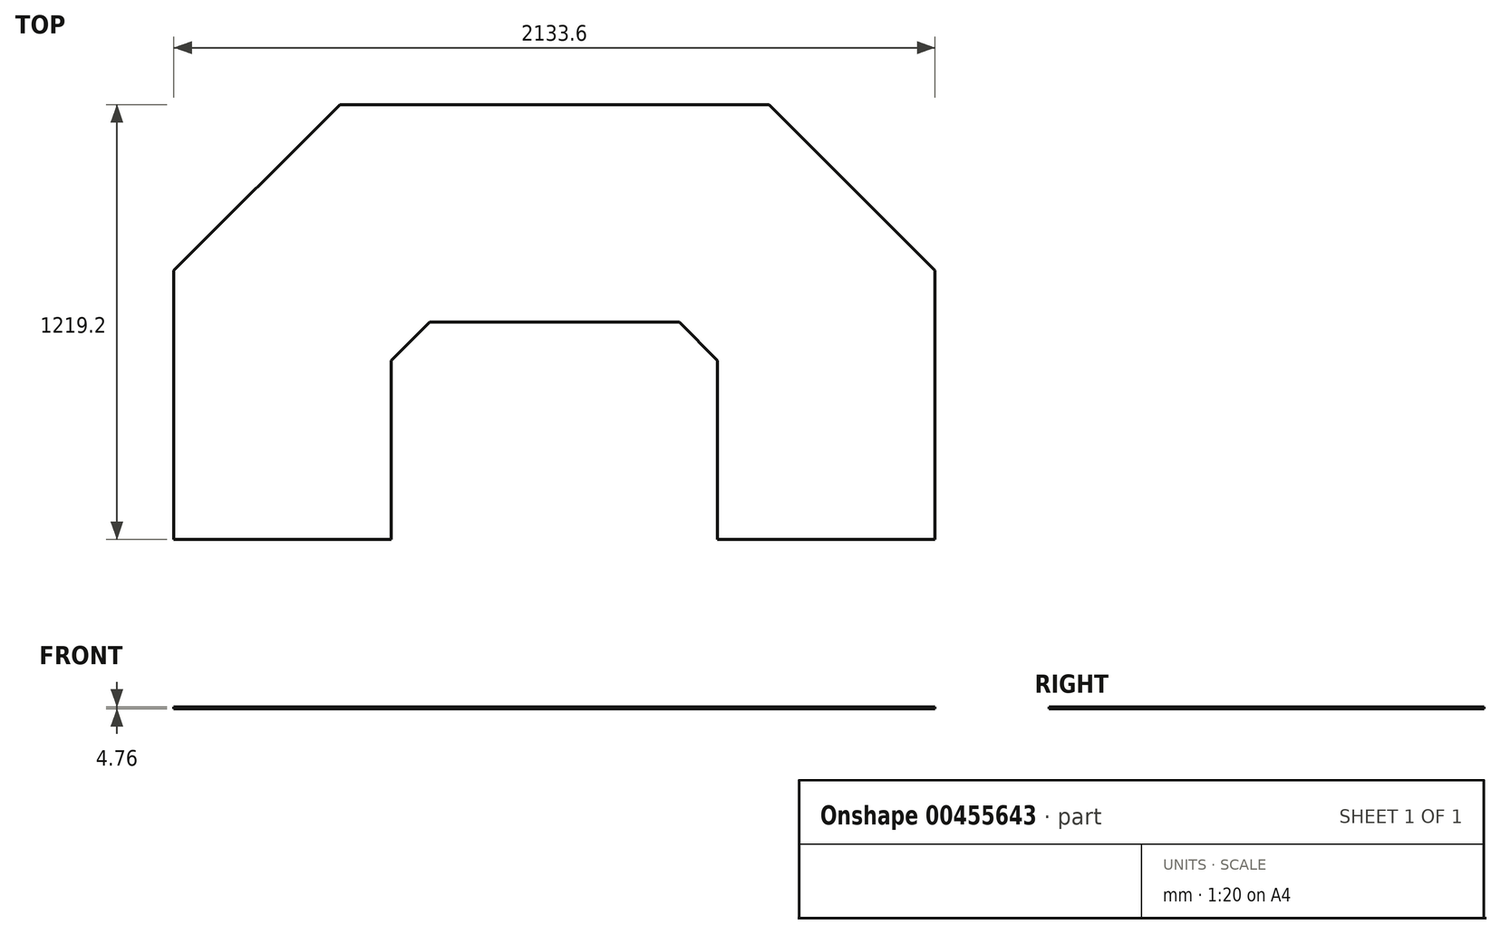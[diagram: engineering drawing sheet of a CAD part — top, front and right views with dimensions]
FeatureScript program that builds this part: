
annotation { "Feature Type Name" : "Feature", "Feature Type Description" : "" }
export const myFeature = defineFeature(function(context is Context, id is Id, definition is map)
    precondition{}
    {
        {
            var Q0;
            Q0=qCreatedBy(makeId("Top.planeOp"),FACE);
            var sketch = newSketch(context, id + "F0", { "sketchPlane" : qUnion([Q0])});
            skLineSegment(sketch, "E0", {"start": v(-601.94, 609.6) * mm, "end": v(0, 609.6) * mm});
            skLineSegment(sketch, "E1", {"start": v(-1066.8, 144.74) * mm, "end": v(-601.94, 609.6) * mm});
            skLineSegment(sketch, "E2", {"start": v(-1066.8, 144.74) * mm, "end": v(-1066.8, -609.6) * mm});
            skLineSegment(sketch, "E3", {"start": v(-1066.8, -609.6) * mm, "end": v(-457.2, -609.6) * mm});
            skLineSegment(sketch, "E4", {"start": v(-457.2, -609.6) * mm, "end": v(-457.2, -107.76) * mm});
            skLineSegment(sketch, "E5", {"start": v(-349.44, 0) * mm, "end": v(0, 0) * mm});
            skLineSegment(sketch, "E6", {"start": v(0, 0) * mm, "end": v(0, 609.6) * mm, "construction": true});
            skLineSegment(sketch, "E7.MirrorCS", {"start": v(1066.8, 144.74) * mm, "end": v(601.94, 609.6) * mm});
            skLineSegment(sketch, "E8.MirrorCS", {"start": v(601.94, 609.6) * mm, "end": v(0, 609.6) * mm});
            skLineSegment(sketch, "E9.MirrorCS", {"start": v(457.2, -609.6) * mm, "end": v(457.2, -107.76) * mm});
            skLineSegment(sketch, "E10.MirrorCS", {"start": v(1066.8, -609.6) * mm, "end": v(457.2, -609.6) * mm});
            skLineSegment(sketch, "E11.MirrorCS", {"start": v(1066.8, 144.74) * mm, "end": v(1066.8, -609.6) * mm});
            skLineSegment(sketch, "E12.MirrorCS", {"start": v(349.44, 0) * mm, "end": v(0, 0) * mm});
            skLineSegment(sketch, "E13", {"start": v(349.44, 0) * mm, "end": v(457.2, -107.76) * mm});
            skLineSegment(sketch, "E14", {"start": v(-457.2, -107.76) * mm, "end": v(-349.44, 0) * mm});
            skSolve(sketch);
        }
        {
            var Q0;
            Q0=makeQuery(id+"F0.imprint","IMPRINT",FACE,{"disambiguationData":[TD([[makeQuery(id+"F0.imprint","IMPRINT",EDGE,{"derivedFrom":sQuery(id+"F0.wireOp",EDGE,"E0")}),-1.0]])]});
            extrude(context, id + "F1", {"entities" : qUnion([Q0]), "depth" : 4.76 * mm});
        }
    });
